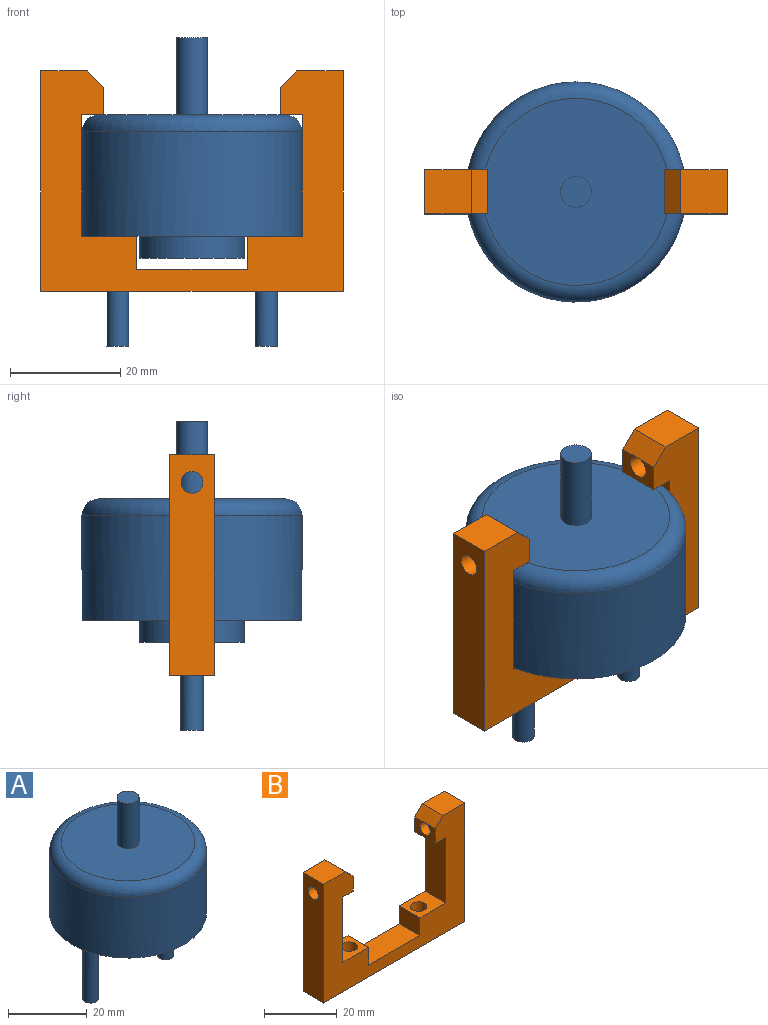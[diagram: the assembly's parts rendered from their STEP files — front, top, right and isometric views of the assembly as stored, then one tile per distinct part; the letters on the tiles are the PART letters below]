
ASSEMBLY  parts=2 mates=1
PART A: 12 faces, bbox 43.3x43.3x56 mm
  f0: cylinder r=20mm len=40mm, axis (0,0,1), area 2387.6mm2, adj f6,f11
  f1: plane 34x34mm, normal (0,0,1), area 883.3mm2, adj f2,f11
  f2: cylinder r=2.8mm len=14mm, axis (0,0,1), area 246.3mm2, adj f1,f3
  f3: plane 5.6x5.6mm, normal (0,0,1), area 24.6mm2, adj f2
  f4: plane 19x19mm, normal (0,0,-1), area 283.5mm2, adj f5
  f5: cylinder r=9.5mm len=19mm, axis (0,0,1), area 238.8mm2, adj f4,f6
  f6: plane 40x40mm, normal (0,0,-1), area 948mm2, adj f0,f5,f7,f9
  f7: cylinder r=2mm len=20mm, axis (0,0,1), area 251.3mm2, adj f6,f8
  f8: plane 4x4mm, normal (0,0,-1), area 12.6mm2, adj f7
  f9: cylinder r=2mm len=20mm, axis (0,0,1), area 251.3mm2, adj f6,f10
  f10: plane 4x4mm, normal (0,0,-1), area 12.6mm2, adj f9
  f11: torus R=17mm, axis (0,0,-1), area 559.9mm2, adj f0,f1
PART B: 24 faces, bbox 55x8x40 mm
  f0: plane 22x8mm, normal (-1,0,0), area 176mm2, adj f7,f12,f13,f19
  f1: plane 22x8mm, normal (1,0,0), area 176mm2, adj f11,f12,f13,f16
  f2: plane 8.5x8mm, normal (0,0,1), area 68mm2, adj f3,f12,f13,f23
  f3: plane 40x8mm, normal (-1,0,0), area 307.4mm2, adj f2,f4,f12,f13,f21
  f4: plane 55x8mm, normal (0,0,-1), area 408.2mm2, adj f3,f5,f12,f13,f14,f15
  f5: plane 40x8mm, normal (1,0,0), area 307.4mm2, adj f4,f6,f12,f13,f20
  f6: plane 8.5x8mm, normal (0,0,1), area 68mm2, adj f5,f12,f13,f22
  f7: plane 10x8mm, normal (0,0,1), area 64.1mm2, adj f0,f8,f12,f13,f15
  f8: plane 8x6mm, normal (-1,0,0), area 48mm2, adj f7,f9,f12,f13
  f9: plane 20x8mm, normal (0,0,1), area 160mm2, adj f8,f10,f12,f13
  f10: plane 8x6mm, normal (1,0,0), area 48mm2, adj f9,f11,f12,f13
  f11: plane 10x8mm, normal (0,0,1), area 64.1mm2, adj f1,f10,f12,f13,f14
  f12: plane 55x40mm, normal (0,-1,0), area 935mm2, adj f0,f1,f2,f3,f4,f5,f6,f7
  f13: plane 55x40mm, normal (0,1,0), area 935mm2, adj f0,f1,f2,f3,f4,f5,f6,f7
  f14: cylinder r=2.25mm len=10mm, axis (0,0,-1), area 141.4mm2, adj f4,f11
  f15: cylinder r=2.25mm len=10mm, axis (0,0,-1), area 141.4mm2, adj f4,f7
  f16: plane 8x4mm, normal (0,0,-1), area 32mm2, adj f1,f12,f13,f17
  f17: plane 8x5mm, normal (1,0,0), area 27.4mm2, adj f12,f13,f16,f21,f23
  f18: plane 8x5mm, normal (-1,0,0), area 27.4mm2, adj f12,f13,f19,f20,f22
  f19: plane 8x4mm, normal (0,0,-1), area 32mm2, adj f0,f12,f13,f18
  f20: cylinder r=2mm len=11.5mm, axis (-1,0,0), area 144.5mm2, adj f5,f18
  f21: cylinder r=2mm len=11.5mm, axis (-1,0,0), area 144.5mm2, adj f3,f17
  f22: plane 8x3mm, normal (-0.71,0,0.71), area 33.9mm2, adj f6,f12,f13,f18
  f23: plane 8x3mm, normal (0.71,0,0.71), area 33.9mm2, adj f2,f12,f13,f17
PLACE A at identity fixed
PLACE B t=(0,0,14)mm
MATE fastened B.f14 <-> A.f7  axis (0,0,1) through (-13.5,0,4)mm
